FCSTD DOCUMENT  (FreeCAD 0.16R6706 (Git))
Label: KNX_2Taster_mit_Display_CCS_Tasterwippe
License: All rights reserved
LicenseURL: http://en.wikipedia.org/wiki/All_rights_reserved
objects: Sketcher::SketchObject×1
note: 1 computed .brp shape members not serialized (recipe doc carries the construction recipe); baked Part::Feature solids carry a one-line shape summary decoded from their .brp

FEATURE [Sketcher::SketchObject] Sketch
  sketch-geometry (136):
    g0: LineSegment StartX=2.17451 StartY=2.3051 StartZ=0 EndX=56.0745 EndY=2.3051 EndZ=0
    g1: LineSegment StartX=0.874504 StartY=3.6051 StartZ=0 EndX=0.874504 EndY=20.9051 EndZ=0
    g2: ArcOfCircle CenterX=2.1745 CenterY=3.6051 CenterZ=0 NormalX=0 NormalY=0 NormalZ=1 Radius=1.3 StartAngle=3.14159 EndAngle=4.71239
    g3: LineSegment StartX=57.3745 StartY=3.6051 StartZ=0 EndX=57.3745 EndY=20.9051 EndZ=0
    g4: LineSegment StartX=0.874504 StartY=20.9051 StartZ=0 EndX=57.3745 EndY=20.9051 EndZ=0
    g5: ArcOfCircle CenterX=56.0745 CenterY=3.6051 CenterZ=0 NormalX=0 NormalY=0 NormalZ=1 Radius=1.3 StartAngle=4.71239 EndAngle=6.28318
    g6: GeomPoint [constr] X=36.4745 Y=11.6051 Z=0
    g7: Circle [constr] CenterX=36.4745 CenterY=11.6051 CenterZ=0 NormalX=0 NormalY=0 NormalZ=1 Radius=4.5
    g8: Circle [constr] CenterX=36.4745 CenterY=11.6051 CenterZ=0 NormalX=0 NormalY=0 NormalZ=1 Radius=3
    g9: Circle [constr] CenterX=36.4745 CenterY=11.6051 CenterZ=0 NormalX=0 NormalY=0 NormalZ=1 Radius=1.5
    g10: LineSegment [constr] StartX=36.4745 StartY=11.6051 StartZ=0 EndX=37.9745 EndY=11.6051 EndZ=0
    g11: LineSegment [constr] StartX=36.4745 StartY=11.6051 StartZ=0 EndX=36.4745 EndY=10.1051 EndZ=0
    g12: LineSegment [constr] StartX=36.4745 StartY=11.6051 StartZ=0 EndX=34.9745 EndY=11.6051 EndZ=0
    g13: LineSegment [constr] StartX=36.4745 StartY=11.6051 StartZ=0 EndX=36.4745 EndY=13.1051 EndZ=0
    g14: LineSegment [constr] StartX=36.4745 StartY=11.6051 StartZ=0 EndX=37.3524 EndY=16.0186 EndZ=0
    g15: LineSegment [constr] StartX=36.4745 StartY=11.6051 StartZ=0 EndX=38.9746 EndY=15.3467 EndZ=0
    g16: LineSegment [constr] StartX=36.4745 StartY=11.6051 StartZ=0 EndX=40.888 EndY=12.483 EndZ=0
    g17: LineSegment [constr] StartX=36.4745 StartY=11.6051 StartZ=0 EndX=40.2161 EndY=14.1052 EndZ=0
    g18: GeomPoint [constr] X=36.4745 Y=11.6051 Z=0
    g19: GeomPoint [constr] X=36.4745 Y=11.6051 Z=0
    g20: GeomPoint [constr] X=36.4745 Y=11.6051 Z=0
    g21: LineSegment [constr] StartX=36.4745 StartY=11.6051 StartZ=0 EndX=40.888 EndY=10.7272 EndZ=0
    g22: LineSegment [constr] StartX=36.4745 StartY=11.6051 StartZ=0 EndX=40.2161 EndY=9.10503 EndZ=0
    g23: LineSegment [constr] StartX=36.4745 StartY=11.6051 StartZ=0 EndX=38.9746 EndY=7.86349 EndZ=0
    g24: LineSegment [constr] StartX=36.4745 StartY=11.6051 StartZ=0 EndX=37.3524 EndY=7.19157 EndZ=0
    g25: LineSegment [constr] StartX=36.4745 StartY=11.6051 StartZ=0 EndX=37.6226 EndY=14.3767 EndZ=0
    g26: LineSegment [constr] StartX=36.4745 StartY=11.6051 StartZ=0 EndX=39.2461 EndY=12.7531 EndZ=0
    g27: LineSegment [constr] StartX=36.4745 StartY=11.6051 StartZ=0 EndX=39.2461 EndY=10.457 EndZ=0
    g28: LineSegment [constr] StartX=36.4745 StartY=11.6051 StartZ=0 EndX=37.6226 EndY=8.83346 EndZ=0
    g29: LineSegment [constr] StartX=36.4745 StartY=11.6051 StartZ=0 EndX=35.5966 EndY=7.19157 EndZ=0
    g30: LineSegment [constr] StartX=36.4745 StartY=11.6051 StartZ=0 EndX=33.9744 EndY=7.86349 EndZ=0
    g31: LineSegment [constr] StartX=36.4745 StartY=11.6051 StartZ=0 EndX=32.7329 EndY=9.10503 EndZ=0
    g32: LineSegment [constr] StartX=36.4745 StartY=11.6051 StartZ=0 EndX=32.061 EndY=10.7272 EndZ=0
    g33: LineSegment [constr] StartX=36.4745 StartY=11.6051 StartZ=0 EndX=32.061 EndY=12.483 EndZ=0
    g34: LineSegment [constr] StartX=36.4745 StartY=11.6051 StartZ=0 EndX=32.7329 EndY=14.1052 EndZ=0
    g35: LineSegment [constr] StartX=36.4745 StartY=11.6051 StartZ=0 EndX=33.9744 EndY=15.3467 EndZ=0
    g36: LineSegment [constr] StartX=36.4745 StartY=11.6051 StartZ=0 EndX=35.5966 EndY=16.0186 EndZ=0
    g37: LineSegment [constr] StartX=36.4745 StartY=11.6051 StartZ=0 EndX=35.3265 EndY=14.3767 EndZ=0
    g38: LineSegment [constr] StartX=36.4745 StartY=11.6051 StartZ=0 EndX=33.7029 EndY=12.7531 EndZ=0
    g39: LineSegment [constr] StartX=36.4745 StartY=11.6051 StartZ=0 EndX=33.7029 EndY=10.457 EndZ=0
    g40: LineSegment [constr] StartX=36.4745 StartY=11.6051 StartZ=0 EndX=35.3265 EndY=8.83346 EndZ=0
    g41: Circle CenterX=35.3265 CenterY=14.3767 CenterZ=0 NormalX=0 NormalY=0 NormalZ=1 Radius=0.5
    g42: Circle CenterX=35.5966 CenterY=16.0186 CenterZ=0 NormalX=0 NormalY=0 NormalZ=1 Radius=0.5
    g43: Circle CenterX=37.3524 CenterY=16.0186 CenterZ=0 NormalX=0 NormalY=0 NormalZ=1 Radius=0.5
    g44: Circle CenterX=38.9746 CenterY=15.3467 CenterZ=0 NormalX=0 NormalY=0 NormalZ=1 Radius=0.5
    g45: Circle CenterX=40.2161 CenterY=14.1052 CenterZ=0 NormalX=0 NormalY=0 NormalZ=1 Radius=0.5
    g46: Circle CenterX=37.6226 CenterY=14.3767 CenterZ=0 NormalX=0 NormalY=0 NormalZ=1 Radius=0.5
    g47: Circle CenterX=39.2461 CenterY=12.7531 CenterZ=0 NormalX=0 NormalY=0 NormalZ=1 Radius=0.5
    g48: Circle CenterX=40.888 CenterY=12.483 CenterZ=0 NormalX=0 NormalY=0 NormalZ=1 Radius=0.5
    g49: Circle CenterX=40.888 CenterY=10.7272 CenterZ=0 NormalX=0 NormalY=0 NormalZ=1 Radius=0.5
    g50: Circle CenterX=39.2461 CenterY=10.457 CenterZ=0 NormalX=0 NormalY=0 NormalZ=1 Radius=0.5
    g51: Circle CenterX=40.2161 CenterY=9.10503 CenterZ=0 NormalX=0 NormalY=0 NormalZ=1 Radius=0.5
    g52: Circle CenterX=38.9746 CenterY=7.86349 CenterZ=0 NormalX=0 NormalY=0 NormalZ=1 Radius=0.5
    g53: Circle CenterX=37.3524 CenterY=7.19157 CenterZ=0 NormalX=0 NormalY=0 NormalZ=1 Radius=0.5
    g54: Circle CenterX=37.6226 CenterY=8.83346 CenterZ=0 NormalX=0 NormalY=0 NormalZ=1 Radius=0.5
    g55: Circle CenterX=35.3265 CenterY=8.83346 CenterZ=0 NormalX=0 NormalY=0 NormalZ=1 Radius=0.5
    g56: Circle CenterX=35.5966 CenterY=7.19157 CenterZ=0 NormalX=0 NormalY=0 NormalZ=1 Radius=0.5
    g57: Circle CenterX=33.9744 CenterY=7.86349 CenterZ=0 NormalX=0 NormalY=0 NormalZ=1 Radius=0.5
    g58: Circle CenterX=32.7329 CenterY=9.10503 CenterZ=0 NormalX=0 NormalY=0 NormalZ=1 Radius=0.5
    g59: Circle CenterX=33.7029 CenterY=10.457 CenterZ=0 NormalX=0 NormalY=0 NormalZ=1 Radius=0.5
    g60: Circle [constr] CenterX=32.061 CenterY=10.7272 CenterZ=0 NormalX=0 NormalY=0 NormalZ=1 Radius=0
    g61: Circle CenterX=32.061 CenterY=12.483 CenterZ=0 NormalX=0 NormalY=0 NormalZ=1 Radius=0.5
    g62: Circle CenterX=33.7029 CenterY=12.7531 CenterZ=0 NormalX=0 NormalY=0 NormalZ=1 Radius=0.5
    g63: Circle CenterX=32.7329 CenterY=14.1052 CenterZ=0 NormalX=0 NormalY=0 NormalZ=1 Radius=0.5
    g64: Circle CenterX=33.9744 CenterY=15.3467 CenterZ=0 NormalX=0 NormalY=0 NormalZ=1 Radius=0.5
    g65: Circle CenterX=36.4745 CenterY=13.1051 CenterZ=0 NormalX=0 NormalY=0 NormalZ=1 Radius=0.5
    g66: Circle CenterX=37.9745 CenterY=11.6051 CenterZ=0 NormalX=0 NormalY=0 NormalZ=1 Radius=0.5
    g67: Circle CenterX=36.4745 CenterY=10.1051 CenterZ=0 NormalX=0 NormalY=0 NormalZ=1 Radius=0.5
    g68: Circle CenterX=32.061 CenterY=10.7272 CenterZ=0 NormalX=0 NormalY=0 NormalZ=1 Radius=0.5
    g69: Circle CenterX=36.4745 CenterY=11.6051 CenterZ=0 NormalX=0 NormalY=0 NormalZ=1 Radius=0.5
    g70: Circle CenterX=34.9745 CenterY=11.6051 CenterZ=0 NormalX=0 NormalY=0 NormalZ=1 Radius=0.5
    g71: GeomPoint [constr] X=21.7745 Y=11.6051 Z=0
    g72: Circle [constr] CenterX=21.7745 CenterY=11.6051 CenterZ=0 NormalX=0 NormalY=0 NormalZ=1 Radius=4.5
    g73: Circle [constr] CenterX=21.7745 CenterY=11.6051 CenterZ=0 NormalX=0 NormalY=0 NormalZ=1 Radius=3
    g74: Circle [constr] CenterX=21.7745 CenterY=11.6051 CenterZ=0 NormalX=0 NormalY=0 NormalZ=1 Radius=1.5
    g75: LineSegment [constr] StartX=21.7745 StartY=11.6051 StartZ=0 EndX=23.2745 EndY=11.6051 EndZ=0
    g76: LineSegment [constr] StartX=21.7745 StartY=11.6051 StartZ=0 EndX=21.7745 EndY=10.1051 EndZ=0
    g77: LineSegment [constr] StartX=21.7745 StartY=11.6051 StartZ=0 EndX=20.2745 EndY=11.6051 EndZ=0
    g78: LineSegment [constr] StartX=21.7745 StartY=11.6051 StartZ=0 EndX=21.7745 EndY=13.1051 EndZ=0
    g79: LineSegment [constr] StartX=21.7745 StartY=11.6051 StartZ=0 EndX=22.6524 EndY=16.0186 EndZ=0
    g80: LineSegment [constr] StartX=21.7745 StartY=11.6051 StartZ=0 EndX=24.2746 EndY=15.3467 EndZ=0
    g81: LineSegment [constr] StartX=21.7745 StartY=11.6051 StartZ=0 EndX=26.188 EndY=12.483 EndZ=0
    g82: LineSegment [constr] StartX=21.7745 StartY=11.6051 StartZ=0 EndX=25.5161 EndY=14.1052 EndZ=0
    g83: GeomPoint [constr] X=21.7745 Y=11.6051 Z=0
    g84: GeomPoint [constr] X=21.7745 Y=11.6051 Z=0
    g85: GeomPoint [constr] X=21.7745 Y=11.6051 Z=0
    g86: LineSegment [constr] StartX=21.7745 StartY=11.6051 StartZ=0 EndX=26.188 EndY=10.7272 EndZ=0
    g87: LineSegment [constr] StartX=21.7745 StartY=11.6051 StartZ=0 EndX=25.5161 EndY=9.10503 EndZ=0
    g88: LineSegment [constr] StartX=21.7745 StartY=11.6051 StartZ=0 EndX=24.2746 EndY=7.86349 EndZ=0
    g89: LineSegment [constr] StartX=21.7745 StartY=11.6051 StartZ=0 EndX=22.6524 EndY=7.19157 EndZ=0
    g90: LineSegment [constr] StartX=21.7745 StartY=11.6051 StartZ=0 EndX=22.9226 EndY=14.3767 EndZ=0
    g91: LineSegment [constr] StartX=21.7745 StartY=11.6051 StartZ=0 EndX=24.5461 EndY=12.7531 EndZ=0
    g92: LineSegment [constr] StartX=21.7745 StartY=11.6051 StartZ=0 EndX=24.5461 EndY=10.457 EndZ=0
    g93: LineSegment [constr] StartX=21.7745 StartY=11.6051 StartZ=0 EndX=22.9226 EndY=8.83346 EndZ=0
    g94: LineSegment [constr] StartX=21.7745 StartY=11.6051 StartZ=0 EndX=20.8966 EndY=7.19157 EndZ=0
    g95: LineSegment [constr] StartX=21.7745 StartY=11.6051 StartZ=0 EndX=19.2744 EndY=7.86349 EndZ=0
    g96: LineSegment [constr] StartX=21.7745 StartY=11.6051 StartZ=0 EndX=18.0329 EndY=9.10503 EndZ=0
    g97: LineSegment [constr] StartX=21.7745 StartY=11.6051 StartZ=0 EndX=17.361 EndY=10.7272 EndZ=0
    g98: LineSegment [constr] StartX=21.7745 StartY=11.6051 StartZ=0 EndX=17.361 EndY=12.483 EndZ=0
    g99: LineSegment [constr] StartX=21.7745 StartY=11.6051 StartZ=0 EndX=18.0329 EndY=14.1052 EndZ=0
    g100: LineSegment [constr] StartX=21.7745 StartY=11.6051 StartZ=0 EndX=19.2744 EndY=15.3467 EndZ=0
    g101: LineSegment [constr] StartX=21.7745 StartY=11.6051 StartZ=0 EndX=20.8966 EndY=16.0186 EndZ=0
    g102: LineSegment [constr] StartX=21.7745 StartY=11.6051 StartZ=0 EndX=20.6265 EndY=14.3767 EndZ=0
    g103: LineSegment [constr] StartX=21.7745 StartY=11.6051 StartZ=0 EndX=19.0029 EndY=12.7531 EndZ=0
    g104: LineSegment [constr] StartX=21.7745 StartY=11.6051 StartZ=0 EndX=19.0029 EndY=10.457 EndZ=0
    g105: LineSegment [constr] StartX=21.7745 StartY=11.6051 StartZ=0 EndX=20.6265 EndY=8.83346 EndZ=0
    g106: Circle CenterX=20.6265 CenterY=14.3767 CenterZ=0 NormalX=0 NormalY=0 NormalZ=1 Radius=0.5
    g107: Circle CenterX=20.8966 CenterY=16.0186 CenterZ=0 NormalX=0 NormalY=0 NormalZ=1 Radius=0.5
    g108: Circle CenterX=22.6524 CenterY=16.0186 CenterZ=0 NormalX=0 NormalY=0 NormalZ=1 Radius=0.5
    g109: Circle CenterX=24.2746 CenterY=15.3467 CenterZ=0 NormalX=0 NormalY=0 NormalZ=1 Radius=0.5
    g110: Circle CenterX=25.5161 CenterY=14.1052 CenterZ=0 NormalX=0 NormalY=0 NormalZ=1 Radius=0.5
    g111: Circle CenterX=22.9226 CenterY=14.3767 CenterZ=0 NormalX=0 NormalY=0 NormalZ=1 Radius=0.5
    g112: Circle CenterX=24.5461 CenterY=12.7531 CenterZ=0 NormalX=0 NormalY=0 NormalZ=1 Radius=0.5
    g113: Circle CenterX=26.188 CenterY=12.483 CenterZ=0 NormalX=0 NormalY=0 NormalZ=1 Radius=0.5
    g114: Circle CenterX=26.188 CenterY=10.7272 CenterZ=0 NormalX=0 NormalY=0 NormalZ=1 Radius=0.5
    g115: Circle CenterX=24.5461 CenterY=10.457 CenterZ=0 NormalX=0 NormalY=0 NormalZ=1 Radius=0.5
    g116: Circle CenterX=25.5161 CenterY=9.10503 CenterZ=0 NormalX=0 NormalY=0 NormalZ=1 Radius=0.5
    g117: Circle CenterX=24.2746 CenterY=7.86349 CenterZ=0 NormalX=0 NormalY=0 NormalZ=1 Radius=0.5
    g118: Circle CenterX=22.6524 CenterY=7.19157 CenterZ=0 NormalX=0 NormalY=0 NormalZ=1 Radius=0.5
    g119: Circle CenterX=22.9226 CenterY=8.83346 CenterZ=0 NormalX=0 NormalY=0 NormalZ=1 Radius=0.5
    g120: Circle CenterX=20.6265 CenterY=8.83346 CenterZ=0 NormalX=0 NormalY=0 NormalZ=1 Radius=0.5
    g121: Circle CenterX=20.8966 CenterY=7.19157 CenterZ=0 NormalX=0 NormalY=0 NormalZ=1 Radius=0.5
    g122: Circle CenterX=19.2744 CenterY=7.86349 CenterZ=0 NormalX=0 NormalY=0 NormalZ=1 Radius=0.5
    g123: Circle CenterX=18.0329 CenterY=9.10503 CenterZ=0 NormalX=0 NormalY=0 NormalZ=1 Radius=0.5
    g124: Circle CenterX=19.0029 CenterY=10.457 CenterZ=0 NormalX=0 NormalY=0 NormalZ=1 Radius=0.5
    g125: Circle [constr] CenterX=17.361 CenterY=10.7272 CenterZ=0 NormalX=0 NormalY=0 NormalZ=1 Radius=0
    g126: Circle CenterX=17.361 CenterY=12.483 CenterZ=0 NormalX=0 NormalY=0 NormalZ=1 Radius=0.5
    g127: Circle CenterX=19.0029 CenterY=12.7531 CenterZ=0 NormalX=0 NormalY=0 NormalZ=1 Radius=0.5
    g128: Circle CenterX=18.0329 CenterY=14.1052 CenterZ=0 NormalX=0 NormalY=0 NormalZ=1 Radius=0.5
    g129: Circle CenterX=19.2744 CenterY=15.3467 CenterZ=0 NormalX=0 NormalY=0 NormalZ=1 Radius=0.5
    g130: Circle CenterX=21.7745 CenterY=13.1051 CenterZ=0 NormalX=0 NormalY=0 NormalZ=1 Radius=0.5
    g131: Circle CenterX=23.2745 CenterY=11.6051 CenterZ=0 NormalX=0 NormalY=0 NormalZ=1 Radius=0.5
    g132: Circle CenterX=21.7745 CenterY=10.1051 CenterZ=0 NormalX=0 NormalY=0 NormalZ=1 Radius=0.5
    g133: Circle CenterX=17.361 CenterY=10.7272 CenterZ=0 NormalX=0 NormalY=0 NormalZ=1 Radius=0.5
    g134: Circle CenterX=21.7745 CenterY=11.6051 CenterZ=0 NormalX=0 NormalY=0 NormalZ=1 Radius=0.5
    g135: Circle CenterX=20.2745 CenterY=11.6051 CenterZ=0 NormalX=0 NormalY=0 NormalZ=1 Radius=0.5
  constraints (328):
    c: Horizontal(g0)
    c: Vertical(g1)
    c: Coincident(g2,g1)
    c: Equal(g3,g1)
    c: Coincident(g4,g1)
    c: Coincident(g4,g3)
    c: Parallel(g0,g4)
    c: DistanceX(g4,g4) = 56.5
    c: Tangent(g2,g1)
    c: Coincident(g5,g0)
    c: Tangent(g5,g3)
    c: Tangent(g0,g5)
    c: Coincident(g3,g5)
    c: DistanceX(g6,g3) = 20.9
    c: Coincident(g7,g6)
    c: Coincident(g8,g6)
    c: Coincident(g9,g6)
    c: Radius(g9) = 1.5
    c: Radius(g8) = 3
    c: Radius(g7) = 4.5
    c: PointOnObject(g10,g9)
    c: Horizontal(g10)
    c: Coincident(g11,g6)
    c: PointOnObject(g11,g9)
    c: Vertical(g11)
    c: Coincident(g12,g6)
    c: PointOnObject(g12,g9)
    c: Horizontal(g12)
    c: Coincident(g13,g6)
    c: PointOnObject(g13,g9)
    c: Vertical(g13)
    c: Coincident(g14,g6)
    c: PointOnObject(g14,g7)
    c: Coincident(g15,g10)
    c: PointOnObject(g15,g7)
    c: Coincident(g16,g10)
    c: PointOnObject(g16,g7)
    c: Coincident(g17,g6)
    c: PointOnObject(g17,g7)
    c: Angle(g14) = 1.37445
    c: Angle(g15) = 0.981748
    c: Angle(g16) = 0.19635
    c: Angle(g17) = 0.589049
    c: Coincident(g21,g6)
    c: PointOnObject(g21,g7)
    c: Coincident(g22,g19)
    c: PointOnObject(g22,g7)
    c: Coincident(g23,g19)
    c: PointOnObject(g23,g7)
    c: Coincident(g24,g6)
    c: PointOnObject(g24,g7)
    c: Angle(g21) = -0.19635
    c: Angle(g22) = -0.589049
    c: Angle(g23) = -0.981748
    c: Angle(g24) = -1.37445
    c: Coincident(g6,g10)
    c: Coincident(g6,g18)
    c: Coincident(g6,g19)
    c: Coincident(g6,g20)
    c: Coincident(g25,g6)
    c: PointOnObject(g25,g8)
    c: Coincident(g26,g6)
    c: PointOnObject(g26,g8)
    c: PointOnObject(g27,g8)
    c: PointOnObject(g28,g8)
    c: Angle(g25) = 1.1781
    c: Angle(g26) = 0.392699
    c: Angle(g27) = -0.392699
    c: Angle(g28) = -1.1781
    c: Coincident(g29,g6)
    c: PointOnObject(g29,g7)
    c: Coincident(g30,g6)
    c: PointOnObject(g30,g7)
    c: Coincident(g31,g6)
    c: PointOnObject(g31,g7)
    c: Coincident(g32,g6)
    c: PointOnObject(g32,g7)
    c: Coincident(g33,g6)
    c: PointOnObject(g34,g7)
    c: Coincident(g35,g6)
    c: PointOnObject(g35,g7)
    c: Coincident(g36,g6)
    c: PointOnObject(g36,g7)
    c: PointOnObject(g33,g7)
    c: Coincident(g6,g27)
    c: Coincident(g6,g28)
    c: Coincident(g6,g34)
    c: Angle(g36) = 1.76715
    c: Angle(g35) = 2.15984
    c: Angle(g34) = 2.55254
    c: Angle(g33) = 2.94524
    c: Angle(g32) = -2.94524
    c: Angle(g31) = -2.55254
    c: Angle(g30) = -2.15984
    c: Angle(g29) = -1.76715
    c: Coincident(g37,g6)
    c: PointOnObject(g37,g8)
    c: PointOnObject(g38,g8)
    c: PointOnObject(g39,g8)
    c: PointOnObject(g40,g8)
    c: Coincident(g6,g38)
    c: Coincident(g6,g39)
    c: Coincident(g6,g40)
    c: Angle(g40) = -1.9635
    c: Angle(g39,g27) = 2.35619
    c: Angle(g38) = 2.74889
    c: Angle(g37) = 1.9635
    c: Coincident(g41,g37)
    c: Coincident(g42,g36)
    c: Coincident(g43,g14)
    c: Coincident(g44,g15)
    c: Coincident(g45,g17)
    c: Coincident(g46,g25)
    c: Coincident(g47,g26)
    c: Coincident(g48,g16)
    c: Coincident(g49,g21)
    c: Radius(g42) = 0.5
    c: Coincident(g50,g27)
    c: Coincident(g51,g22)
    c: Coincident(g52,g23)
    c: Coincident(g53,g24)
    c: Coincident(g54,g28)
    c: Coincident(g55,g40)
    c: Coincident(g56,g29)
    c: Coincident(g57,g30)
    c: Coincident(g58,g31)
    c: Coincident(g59,g39)
    c: Coincident(g60,g32)
    c: Tangent(g60,g7)
    c: Coincident(g61,g33)
    c: Coincident(g62,g38)
    c: Coincident(g63,g34)
    c: Coincident(g64,g35)
    c: Coincident(g65,g13)
    c: Coincident(g66,g10)
    c: Coincident(g67,g11)
    c: Coincident(g68,g32)
    c: Coincident(g69,g6)
    c: Equal(g42,g43)
    c: Equal(g43,g44)
    c: Equal(g44,g45)
    c: Equal(g45,g48)
    c: Equal(g48,g49)
    c: Equal(g49,g51)
    c: Equal(g51,g52)
    c: Equal(g52,g53)
    c: Equal(g53,g56)
    c: Equal(g56,g57)
    c: Equal(g57,g58)
    c: Equal(g58,g68)
    c: Equal(g68,g61)
    c: Equal(g61,g63)
    c: Equal(g63,g64)
    c: Equal(g64,g41)
    c: Equal(g41,g46)
    c: Equal(g46,g47)
    c: Equal(g47,g50)
    c: Equal(g50,g54)
    c: Equal(g54,g55)
    c: Equal(g55,g59)
    c: Equal(g59,g62)
    c: Equal(g62,g65)
    c: Equal(g65,g66)
    c: Equal(g66,g67)
    c: Coincident(g70,g12)
    c: Equal(g67,g70)
    c: Equal(g70,g69)
    c: Coincident(g72,g71)
    c: Coincident(g73,g71)
    c: Coincident(g74,g71)
    c: Equal(g9,g74) = 1.5
    c: Equal(g8,g73) = 3
    c: Equal(g7,g72) = 4.5
    c: PointOnObject(g75,g74)
    c: Horizontal(g75)
    c: Coincident(g76,g71)
    c: PointOnObject(g76,g74)
    c: Vertical(g76)
    c: Coincident(g77,g71)
    c: PointOnObject(g77,g74)
    c: Horizontal(g77)
    c: Coincident(g78,g71)
    c: PointOnObject(g78,g74)
    c: Vertical(g78)
    c: Coincident(g79,g71)
    c: PointOnObject(g79,g72)
    c: Coincident(g80,g75)
    c: PointOnObject(g80,g72)
    c: Coincident(g81,g75)
    c: PointOnObject(g81,g72)
    c: Coincident(g82,g71)
    c: PointOnObject(g82,g72)
    c: Parallel(g14,g79) = 1.37445
    c: Parallel(g15,g80) = 0.981748
    c: Parallel(g16,g81) = 0.19635
    c: Parallel(g17,g82) = 0.589049
    c: Coincident(g86,g71)
    c: PointOnObject(g86,g72)
    c: Coincident(g87,g84)
    c: PointOnObject(g87,g72)
    c: Coincident(g88,g84)
    c: PointOnObject(g88,g72)
    c: Coincident(g89,g71)
    c: PointOnObject(g89,g72)
    c: Parallel(g21,g86) = -0.19635
    c: Parallel(g22,g87) = -0.589049
    c: Parallel(g23,g88) = -0.981748
    c: Parallel(g24,g89) = -1.37445
    c: Coincident(g71,g75)
    c: Coincident(g71,g83)
    c: Coincident(g71,g84)
    c: Coincident(g71,g85)
    c: Coincident(g90,g71)
    c: PointOnObject(g90,g73)
    c: Coincident(g91,g71)
    c: PointOnObject(g91,g73)
    c: PointOnObject(g92,g73)
    c: PointOnObject(g93,g73)
    c: Parallel(g25,g90) = 1.1781
    c: Parallel(g26,g91) = 0.392699
    c: Parallel(g27,g92) = -0.392699
    c: Parallel(g28,g93) = -1.1781
    c: Coincident(g94,g71)
    c: PointOnObject(g94,g72)
    c: Coincident(g95,g71)
    c: PointOnObject(g95,g72)
    c: Coincident(g96,g71)
    c: PointOnObject(g96,g72)
    c: Coincident(g97,g71)
    c: PointOnObject(g97,g72)
    c: Coincident(g98,g71)
    c: PointOnObject(g99,g72)
    c: Coincident(g100,g71)
    c: PointOnObject(g100,g72)
    c: Coincident(g101,g71)
    c: PointOnObject(g101,g72)
    c: PointOnObject(g98,g72)
    c: Coincident(g71,g92)
    c: Coincident(g71,g93)
    c: Coincident(g71,g99)
    c: Parallel(g36,g101) = 1.76715
    c: Parallel(g35,g100) = 2.15984
    c: Parallel(g34,g99) = 2.55254
    c: Parallel(g33,g98) = 2.94524
    c: Parallel(g32,g97) = -2.94524
    c: Parallel(g31,g96) = -2.55254
    c: Parallel(g30,g95) = -2.15984
    c: Parallel(g29,g94) = -1.76715
    c: Coincident(g102,g71)
    c: PointOnObject(g102,g73)
    c: PointOnObject(g103,g73)
    c: PointOnObject(g104,g73)
    c: PointOnObject(g105,g73)
    c: Coincident(g71,g103)
    c: Coincident(g71,g104)
    c: Coincident(g71,g105)
    c: Parallel(g40,g105) = -1.9635
    c: Angle(g104,g92) = 2.35619
    c: Parallel(g38,g103) = 2.74889
    c: Parallel(g37,g102) = 1.9635
    c: Coincident(g106,g102)
    c: Coincident(g107,g101)
    c: Coincident(g108,g79)
    c: Coincident(g109,g80)
    c: Coincident(g110,g82)
    c: Coincident(g111,g90)
    c: Coincident(g112,g91)
    c: Coincident(g113,g81)
    c: Coincident(g114,g86)
    c: Equal(g42,g107) = 0.5
    c: Coincident(g115,g92)
    c: Coincident(g116,g87)
    c: Coincident(g117,g88)
    c: Coincident(g118,g89)
    c: Coincident(g119,g93)
    c: Coincident(g120,g105)
    c: Coincident(g121,g94)
    c: Coincident(g122,g95)
    c: Coincident(g123,g96)
    c: Coincident(g124,g104)
    c: Coincident(g125,g97)
    c: Tangent(g125,g72)
    c: Coincident(g126,g98)
    c: Coincident(g127,g103)
    c: Coincident(g128,g99)
    c: Coincident(g129,g100)
    c: Coincident(g130,g78)
    c: Coincident(g131,g75)
    c: Coincident(g132,g76)
    c: Coincident(g133,g97)
    c: Coincident(g134,g71)
    c: Equal(g107,g108)
    c: Equal(g108,g109)
    c: Equal(g109,g110)
    c: Equal(g110,g113)
    c: Equal(g113,g114)
    c: Equal(g114,g116)
    c: Equal(g116,g117)
    c: Equal(g117,g118)
    c: Equal(g118,g121)
    c: Equal(g121,g122)
    c: Equal(g122,g123)
    c: Equal(g123,g133)
    c: Equal(g133,g126)
    c: Equal(g126,g128)
    c: Equal(g128,g129)
    c: Equal(g129,g106)
    c: Equal(g106,g111)
    c: Equal(g111,g112)
    c: Equal(g112,g115)
    c: Equal(g115,g119)
    c: Equal(g119,g120)
    c: Equal(g120,g124)
    c: Equal(g124,g127)
    c: Equal(g127,g130)
    c: Equal(g130,g131)
    c: Equal(g131,g132)
    c: Coincident(g135,g77)
    c: Equal(g132,g135)
    c: Equal(g135,g134)
    c: DistanceX(g1,g71) = 20.9
    c: DistanceY(g6,g3) = 9.3
    c: DistanceY(g71,g1) = 9.3
    c: DistanceY(g0,g3) = 18.6
    c: Coincident(g0,g2)
    c: Tangent(g0,g2)
    c: Radius(g2) = 1.3
    c: Equal(g5,g2)
